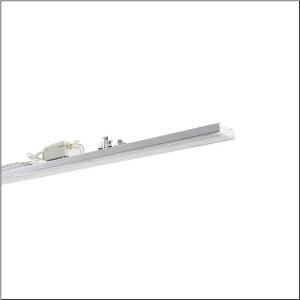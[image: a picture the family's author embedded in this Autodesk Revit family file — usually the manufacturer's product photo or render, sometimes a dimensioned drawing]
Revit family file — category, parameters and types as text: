
# Revit family: licross_r__21_recessed_mo_52te1edv4dxg_57d1
name_source: partatom
category: Lighting Fixtures
units: mm (PartAtom-declared; Revit-internal decimal feet)

## family parameters
Cut with Voids When Loaded = No
Host = Face
Light Source = No
Part Type = Normal
Room Calculation Point = No
Round Connector Dimension = Use Diameter
Shared = No

## types (1)
- --- (1 x LED, 13000 lm, 73.6 W, 4000K)
    Apparent Load = 74 VA
    CIE Flux Codes = 85 95 99 100 100
    Color Rendering = 80
    Color Temperature = 4000K
    Default Elevation = 1800 mm
    Description = Licross® 21 Recessed MO, luminaire insert, of sheet steel, galvanised, coil coated, white, length: 2.250mm, width: 66mm, height: 67mm, LED rated luminous flux: 13.000lm, light colour: 840, control gear: DALI 2, with plug, 5-pole, with phase selection, mains connection: 220..240V, AC, 50/60Hz, rated input power: 74W, halogen-free wiring, primary light control with lens, of plastic, primary optical cover: cover, of PMMA, light emission: direct distribution, primary light characteristic: symmetric, protection rating (complete): IP54, insulation class (complete): insulation class I (protective earthing), certification: CE, ENEC, VDE, UKCA, protection symbol: D if used in an environment with non-conductive dust loads with corresponding accessories, impact resistance: IK06, permissible ambient temperature for indoor applications: -25..+35°C, corresponds to IFS (International Featured Standards) requirements for safety and quality in the food industry, reducing of maximum allowable ambient temperature of 5°C with ceiling mounting, LABS conformity tested according to VDMA 24364:2018-05, packaging unit: 1 piece
    Height = 58 mm
    Lamp = 1 x LED
    Lamp Light Flux = 13000 lm
    Lamp Power = 73.6 W
    Lamp count = 1
    Length = 2250 mm
    Luminous efficacy = 177 lm/W
    Manufacturer = Siteco
    ModVariant = No
    Model = 52TE1EDV4DXG
    Mounting Place = Ceiling
    Mounting Type = Pendant
    Number of Poles = 1
    OnlyDefault = Yes
    Power Factor = 1
    Product Name = Licross® 21 Recessed MO
    Product group = luminaire insert
    ProductGroupID = 901
    Protection Class = Protection class I
    Protection Degree = IP 54
    RLX_Detail_Level = 1
    RLX_Emergency_Light_Flux = 0 lm
    RLX_Emergency_Type = 0
    RLX_Emergency_Type_DB = No
    RlxData = <blob elided: 29413 chars, md5=531a782d>
    Socket = socket
    Standby Power = 0 W
    System Light Flux = 13000 lm
    System Power = 74 W
    Type Comments = factory setting: luminous flux: 100 % | dim-lin: 254 | 336 mA
    Type Image = l_1296930.jpg
    URL = http://relux.com
    VarID = @adj_056999
    Voltage = 0 V
    Weight = 0.00 kg
    Width = 66 mm

## geometry (parser evidence)
native form markers: Blend x4, Sweep x9
no freeform markers — native parametric forms only
